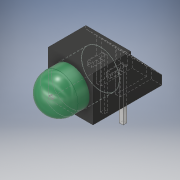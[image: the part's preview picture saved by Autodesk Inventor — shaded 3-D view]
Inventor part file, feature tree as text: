
AUTODESK INVENTOR PART (.ipt)
format: ipt  version: 2019.1 (Build 231200000, 200)  size: 276,480 bytes
history: native  units: mm
features: extrude x7, sketch x7, other x5, fillet x1, mirror x1
ambient origin geometry x8: Origin, YZ Plane, XZ Plane, XY Plane, X Axis, Y Axis, Z Axis, Center Point
bodies: Body1 (feature_tree), Body2 (feature_tree), Body3 (feature_tree)
feature tree (21):
  other  "Plastic"
  extrude  "Выдавливание1"  Depth=0.4mm
  extrude  "Выдавливание2"  Depth=6.0mm
  extrude  "Выдавливание3"  Depth=9.2mm
  extrude  "Выдавливание4"  Depth=6.0mm TaperAngle=0.0deg
  extrude  "Выдавливание5"  Depth=5.1mm
  fillet  "Сопряжение1"  Radius=4.0mm
  other  "РабПлоскость1"
  extrude  "Выдавливание6"  Depth=2.54mm
  mirror  "Зеркальное отражение1"
  extrude  "Выдавливание7"  Depth=0.6mm
  sketch  "Эскиз1"
  other  "Картинка1"
  sketch  "Эскиз2"
  sketch  "Эскиз3"
  sketch  "Эскиз5"
  sketch  "Эскиз6"
  other  "Led"
  sketch  "Эскиз8"
  other  "Led_pin"
  sketch  "Эскиз9"
